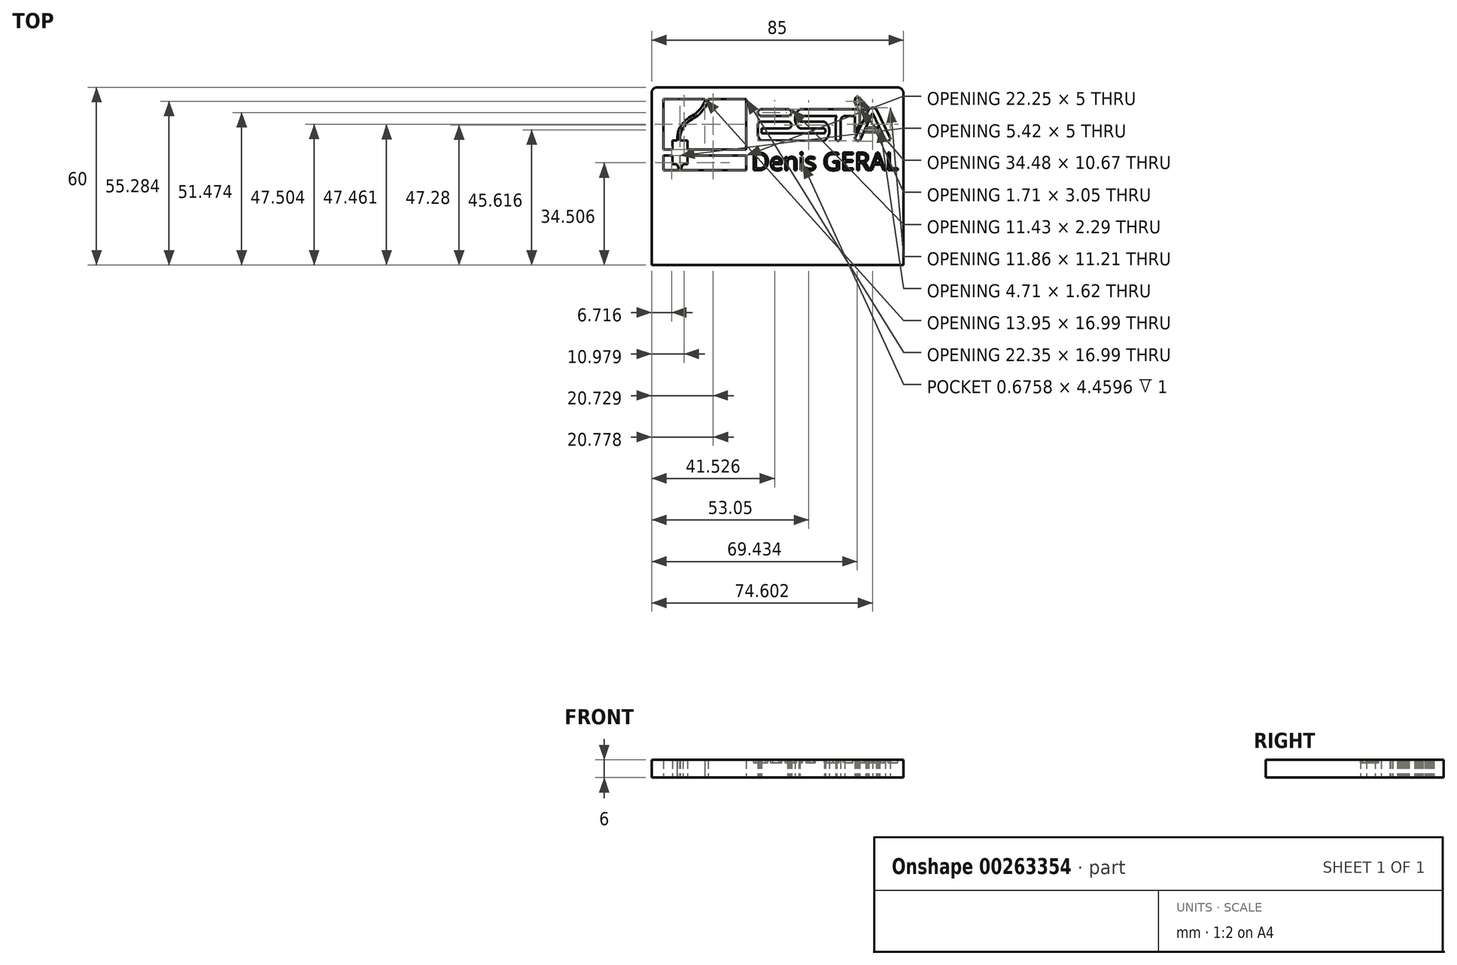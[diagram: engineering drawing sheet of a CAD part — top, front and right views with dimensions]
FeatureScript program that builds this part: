
annotation { "Feature Type Name" : "Feature", "Feature Type Description" : "" }
export const myFeature = defineFeature(function(context is Context, id is Id, definition is map)
    precondition{}
    {
        {
            var Q0;
            Q0=qCreatedBy(makeId("Top.planeOp"),FACE);
            var sketch = newSketch(context, id + "F0", { "sketchPlane" : qUnion([Q0])});
            skLineSegment(sketch, "E0", {"start": v(-259.87, -29.98) * mm, "end": v(-245.92, -29.98) * mm});
            skLineSegment(sketch, "E1", {"start": v(-231.97, -29.98) * mm, "end": v(-231.97, -46.97) * mm});
            skLineSegment(sketch, "E2", {"start": v(-231.97, -46.97) * mm, "end": v(-251.81, -46.97) * mm});
            skLineSegment(sketch, "E3", {"start": v(-251.81, -46.97) * mm, "end": v(-251.81, -43.97) * mm});
            skLineSegment(sketch, "E4", {"start": v(-251.81, -43.97) * mm, "end": v(-254.31, -43.97) * mm});
            skLineSegment(sketch, "E5", {"start": v(-256.81, -43.97) * mm, "end": v(-256.81, -46.97) * mm});
            skLineSegment(sketch, "E6", {"start": v(-256.81, -46.97) * mm, "end": v(-259.87, -46.97) * mm});
            skLineSegment(sketch, "E7", {"start": v(-259.87, -46.97) * mm, "end": v(-259.87, -29.98) * mm});
            skLineSegment(sketch, "E8", {"start": v(-259.87, -48.97) * mm, "end": v(-256.81, -48.97) * mm});
            skLineSegment(sketch, "E9", {"start": v(-256.81, -48.97) * mm, "end": v(-256.81, -51.97) * mm});
            skLineSegment(sketch, "E10", {"start": v(-256.81, -51.97) * mm, "end": v(-255.31, -51.97) * mm});
            skLineSegment(sketch, "E11", {"start": v(-253.31, -51.97) * mm, "end": v(-251.81, -51.97) * mm});
            skLineSegment(sketch, "E12", {"start": v(-251.81, -51.97) * mm, "end": v(-251.81, -48.97) * mm});
            skLineSegment(sketch, "E13", {"start": v(-251.81, -48.97) * mm, "end": v(-231.97, -48.97) * mm});
            skLineSegment(sketch, "E14", {"start": v(-231.97, -48.97) * mm, "end": v(-231.97, -53.97) * mm});
            skLineSegment(sketch, "E15", {"start": v(-259.87, -53.97) * mm, "end": v(-259.87, -48.97) * mm});
            skFitSpline(sketch, "E16", {"points": [v(-255.2, -43.97) * mm, v(-254.45, -39.81) * mm, v(-251.62, -36.46) * mm, v(-248.12, -34) * mm, v(-245.92, -29.98) * mm], "startDerivative": vector(-2.3, 15.03) * mm, "endDerivative": vector(-4.61, 6.78) * mm});
            skFitSpline(sketch, "E17", {"points": [v(-254.31, -43.97) * mm, v(-253.44, -40) * mm, v(-250.75, -37.07) * mm, v(-247.12, -34.45) * mm, v(-244.8, -29.98) * mm], "startDerivative": vector(-2.3, 15.03) * mm, "endDerivative": vector(-4.61, 6.78) * mm});
            skLineSegment(sketch, "E18.bottom", {"start": v(-261.87, -25.98) * mm, "end": v(-180.87, -25.98) * mm});
            skLineSegment(sketch, "E18.top", {"start": v(-263.87, -85.98) * mm, "end": v(-178.87, -85.98) * mm});
            skLineSegment(sketch, "E18.left", {"start": v(-263.87, -27.98) * mm, "end": v(-263.87, -85.98) * mm});
            skLineSegment(sketch, "E18.right", {"start": v(-178.87, -27.98) * mm, "end": v(-178.87, -85.98) * mm});
            skLineSegment(sketch, "E19.trimOffspring", {"start": v(-244.8, -29.98) * mm, "end": v(-231.97, -29.98) * mm});
            skLineSegment(sketch, "E20.trimOffspring", {"start": v(-255.2, -43.97) * mm, "end": v(-256.81, -43.97) * mm});
            skLineSegment(sketch, "E21", {"start": v(-254.31, -53.97) * mm, "end": v(-231.97, -53.97) * mm});
            skLineSegment(sketch, "E22", {"start": v(-254.31, -53.97) * mm, "end": v(-259.87, -53.97) * mm});
            skLineSegment(sketch, "E23.0.0", {"start": v(-226.73, -41.17) * mm, "end": v(-226.73, -39.84) * mm});
            skLineSegment(sketch, "E23.0.1", {"start": v(-226.73, -39.84) * mm, "end": v(-217.96, -39.84) * mm});
            skLineSegment(sketch, "E23.0.2", {"start": v(-217.96, -39.84) * mm, "end": v(-217.85, -39.84) * mm});
            skLineSegment(sketch, "E23.0.3", {"start": v(-217.85, -39.84) * mm, "end": v(-217.73, -39.82) * mm});
            skLineSegment(sketch, "E23.0.4", {"start": v(-217.73, -39.82) * mm, "end": v(-217.62, -39.8) * mm});
            skLineSegment(sketch, "E23.0.5", {"start": v(-217.62, -39.8) * mm, "end": v(-217.5, -39.77) * mm});
            skLineSegment(sketch, "E23.0.6", {"start": v(-217.5, -39.77) * mm, "end": v(-217.4, -39.73) * mm});
            skLineSegment(sketch, "E23.0.7", {"start": v(-217.4, -39.73) * mm, "end": v(-217.3, -39.69) * mm});
            skLineSegment(sketch, "E23.0.8", {"start": v(-217.3, -39.69) * mm, "end": v(-217.2, -39.63) * mm});
            skLineSegment(sketch, "E23.0.9", {"start": v(-217.2, -39.63) * mm, "end": v(-217.1, -39.57) * mm});
            skLineSegment(sketch, "E23.0.10", {"start": v(-217.1, -39.57) * mm, "end": v(-217.02, -39.5) * mm});
            skLineSegment(sketch, "E23.0.11", {"start": v(-217.02, -39.5) * mm, "end": v(-216.94, -39.43) * mm});
            skLineSegment(sketch, "E23.0.12", {"start": v(-216.94, -39.43) * mm, "end": v(-216.87, -39.35) * mm});
            skLineSegment(sketch, "E23.0.13", {"start": v(-216.87, -39.35) * mm, "end": v(-216.8, -39.27) * mm});
            skLineSegment(sketch, "E23.0.14", {"start": v(-216.8, -39.27) * mm, "end": v(-216.75, -39.18) * mm});
            skLineSegment(sketch, "E23.0.15", {"start": v(-216.75, -39.18) * mm, "end": v(-216.7, -39.09) * mm});
            skLineSegment(sketch, "E23.0.16", {"start": v(-216.7, -39.09) * mm, "end": v(-216.67, -39) * mm});
            skLineSegment(sketch, "E23.0.17", {"start": v(-216.67, -39) * mm, "end": v(-216.65, -38.9) * mm});
            skLineSegment(sketch, "E23.0.18", {"start": v(-216.65, -38.9) * mm, "end": v(-216.63, -38.8) * mm});
            skLineSegment(sketch, "E23.0.19", {"start": v(-216.63, -38.8) * mm, "end": v(-216.63, -38.7) * mm});
            skLineSegment(sketch, "E23.0.20", {"start": v(-216.63, -38.7) * mm, "end": v(-216.63, -38.6) * mm});
            skLineSegment(sketch, "E23.0.21", {"start": v(-216.63, -38.6) * mm, "end": v(-216.65, -38.5) * mm});
            skLineSegment(sketch, "E23.0.22", {"start": v(-216.65, -38.5) * mm, "end": v(-216.67, -38.4) * mm});
            skLineSegment(sketch, "E23.0.23", {"start": v(-216.67, -38.4) * mm, "end": v(-216.7, -38.3) * mm});
            skLineSegment(sketch, "E23.0.24", {"start": v(-216.7, -38.3) * mm, "end": v(-216.75, -38.21) * mm});
            skLineSegment(sketch, "E23.0.25", {"start": v(-216.75, -38.21) * mm, "end": v(-216.8, -38.13) * mm});
            skLineSegment(sketch, "E23.0.26", {"start": v(-216.8, -38.13) * mm, "end": v(-216.87, -38.04) * mm});
            skLineSegment(sketch, "E23.0.27", {"start": v(-216.87, -38.04) * mm, "end": v(-216.94, -37.96) * mm});
            skLineSegment(sketch, "E23.0.28", {"start": v(-216.94, -37.96) * mm, "end": v(-217.02, -37.89) * mm});
            skLineSegment(sketch, "E23.0.29", {"start": v(-217.02, -37.89) * mm, "end": v(-217.1, -37.82) * mm});
            skLineSegment(sketch, "E23.0.30", {"start": v(-217.1, -37.82) * mm, "end": v(-217.2, -37.76) * mm});
            skLineSegment(sketch, "E23.0.31", {"start": v(-217.2, -37.76) * mm, "end": v(-217.3, -37.7) * mm});
            skLineSegment(sketch, "E23.0.32", {"start": v(-217.3, -37.7) * mm, "end": v(-217.4, -37.66) * mm});
            skLineSegment(sketch, "E23.0.33", {"start": v(-217.4, -37.66) * mm, "end": v(-217.5, -37.62) * mm});
            skLineSegment(sketch, "E23.0.34", {"start": v(-217.5, -37.62) * mm, "end": v(-217.62, -37.6) * mm});
            skLineSegment(sketch, "E23.0.35", {"start": v(-217.62, -37.6) * mm, "end": v(-217.73, -37.57) * mm});
            skLineSegment(sketch, "E23.0.36", {"start": v(-217.73, -37.57) * mm, "end": v(-217.85, -37.56) * mm});
            skLineSegment(sketch, "E23.0.37", {"start": v(-217.85, -37.56) * mm, "end": v(-217.96, -37.55) * mm});
            skLineSegment(sketch, "E23.0.38", {"start": v(-217.96, -37.55) * mm, "end": v(-226.73, -37.55) * mm});
            skLineSegment(sketch, "E23.0.39", {"start": v(-226.73, -37.55) * mm, "end": v(-226.84, -37.56) * mm});
            skLineSegment(sketch, "E23.0.40", {"start": v(-226.84, -37.56) * mm, "end": v(-226.96, -37.57) * mm});
            skLineSegment(sketch, "E23.0.41", {"start": v(-226.96, -37.57) * mm, "end": v(-227.07, -37.6) * mm});
            skLineSegment(sketch, "E23.0.42", {"start": v(-227.07, -37.6) * mm, "end": v(-227.18, -37.62) * mm});
            skLineSegment(sketch, "E23.0.43", {"start": v(-227.18, -37.62) * mm, "end": v(-227.29, -37.66) * mm});
            skLineSegment(sketch, "E23.0.44", {"start": v(-227.29, -37.66) * mm, "end": v(-227.4, -37.7) * mm});
            skLineSegment(sketch, "E23.0.45", {"start": v(-227.4, -37.7) * mm, "end": v(-227.5, -37.76) * mm});
            skLineSegment(sketch, "E23.0.46", {"start": v(-227.5, -37.76) * mm, "end": v(-227.58, -37.82) * mm});
            skLineSegment(sketch, "E23.0.47", {"start": v(-227.58, -37.82) * mm, "end": v(-227.67, -37.89) * mm});
            skLineSegment(sketch, "E23.0.48", {"start": v(-227.67, -37.89) * mm, "end": v(-227.75, -37.96) * mm});
            skLineSegment(sketch, "E23.0.49", {"start": v(-227.75, -37.96) * mm, "end": v(-227.82, -38.04) * mm});
            skLineSegment(sketch, "E23.0.50", {"start": v(-227.82, -38.04) * mm, "end": v(-227.88, -38.13) * mm});
            skLineSegment(sketch, "E23.0.51", {"start": v(-227.88, -38.13) * mm, "end": v(-227.93, -38.21) * mm});
            skLineSegment(sketch, "E23.0.52", {"start": v(-227.93, -38.21) * mm, "end": v(-227.98, -38.3) * mm});
            skLineSegment(sketch, "E23.0.53", {"start": v(-227.98, -38.3) * mm, "end": v(-228.01, -38.4) * mm});
            skLineSegment(sketch, "E23.0.54", {"start": v(-228.01, -38.4) * mm, "end": v(-228.04, -38.5) * mm});
            skLineSegment(sketch, "E23.0.55", {"start": v(-228.04, -38.5) * mm, "end": v(-228.05, -38.6) * mm});
            skLineSegment(sketch, "E23.0.56", {"start": v(-228.05, -38.6) * mm, "end": v(-228.06, -38.7) * mm});
            skLineSegment(sketch, "E23.0.57", {"start": v(-228.06, -38.7) * mm, "end": v(-228.06, -41.55) * mm});
            skArc(sketch, "E23.0.58", {"start": v(-228.06, -41.55) * mm, "mid": v(-228.06, -41.69) * mm, "end": v(-228.06, -41.82) * mm});
            skArc(sketch, "E23.0.59", {"start": v(-228.06, -41.82) * mm, "mid": v(-227.76, -42.94) * mm, "end": v(-227.01, -43.84) * mm});
            skLineSegment(sketch, "E23.0.60", {"start": v(-227.01, -43.84) * mm, "end": v(-205.58, -44.03) * mm});
            skArc(sketch, "E23.0.61", {"start": v(-205.58, -44.03) * mm, "mid": v(-203.87, -40.8) * mm, "end": v(-205.58, -37.55) * mm});
            skLineSegment(sketch, "E23.0.62", {"start": v(-205.58, -37.55) * mm, "end": v(-213.77, -37.55) * mm});
            skArc(sketch, "E23.0.63", {"start": v(-213.77, -37.55) * mm, "mid": v(-214.15, -36.6) * mm, "end": v(-213.77, -35.65) * mm});
            skLineSegment(sketch, "E23.0.64", {"start": v(-213.77, -35.65) * mm, "end": v(-201.39, -35.65) * mm});
            skArc(sketch, "E23.0.65", {"start": v(-201.39, -35.65) * mm, "mid": v(-201.71, -36.57) * mm, "end": v(-201.77, -37.55) * mm});
            skLineSegment(sketch, "E23.0.66", {"start": v(-201.77, -37.55) * mm, "end": v(-201.77, -43.08) * mm});
            skArc(sketch, "E23.0.67", {"start": v(-201.77, -43.08) * mm, "mid": v(-200.91, -44.04) * mm, "end": v(-200.06, -43.08) * mm});
            skLineSegment(sketch, "E23.0.68", {"start": v(-200.06, -43.08) * mm, "end": v(-200.06, -37.55) * mm});
            skArc(sketch, "E23.0.69", {"start": v(-200.06, -37.55) * mm, "mid": v(-199.78, -36.33) * mm, "end": v(-198.72, -35.65) * mm});
            skLineSegment(sketch, "E23.0.70", {"start": v(-198.72, -35.65) * mm, "end": v(-195.3, -35.65) * mm});
            skLineSegment(sketch, "E23.0.71", {"start": v(-195.3, -35.65) * mm, "end": v(-195.3, -40.41) * mm});
            skArc(sketch, "E23.0.72", {"start": v(-195.3, -40.41) * mm, "mid": v(-195.26, -40.9) * mm, "end": v(-195.1, -41.35) * mm});
            skLineSegment(sketch, "E23.0.73", {"start": v(-195.1, -41.35) * mm, "end": v(-193.58, -38.13) * mm});
            skLineSegment(sketch, "E23.0.74", {"start": v(-193.58, -38.13) * mm, "end": v(-193.58, -34.32) * mm});
            skArc(sketch, "E23.0.75", {"start": v(-193.58, -34.32) * mm, "mid": v(-193.86, -33.64) * mm, "end": v(-194.53, -33.36) * mm});
            skLineSegment(sketch, "E23.0.76", {"start": v(-194.53, -33.36) * mm, "end": v(-213.77, -33.36) * mm});
            skArc(sketch, "E23.0.77", {"start": v(-213.77, -33.36) * mm, "mid": v(-215.49, -36.6) * mm, "end": v(-213.77, -39.84) * mm});
            skLineSegment(sketch, "E23.0.78", {"start": v(-213.77, -39.84) * mm, "end": v(-205.58, -39.84) * mm});
            skArc(sketch, "E23.0.79", {"start": v(-205.58, -39.84) * mm, "mid": v(-205.2, -40.7) * mm, "end": v(-205.58, -41.55) * mm});
            skLineSegment(sketch, "E23.0.80", {"start": v(-205.58, -41.55) * mm, "end": v(-226.34, -41.55) * mm});
            skArc(sketch, "E23.0.81", {"start": v(-226.34, -41.55) * mm, "mid": v(-226.61, -41.44) * mm, "end": v(-226.73, -41.17) * mm});
            skLineSegment(sketch, "E24.0.0", {"start": v(-193.58, -30.54) * mm, "end": v(-193.6, -30.4) * mm});
            skLineSegment(sketch, "E24.0.1", {"start": v(-193.6, -30.4) * mm, "end": v(-193.61, -30.28) * mm});
            skLineSegment(sketch, "E24.0.2", {"start": v(-193.61, -30.28) * mm, "end": v(-193.63, -30.15) * mm});
            skLineSegment(sketch, "E24.0.3", {"start": v(-193.63, -30.15) * mm, "end": v(-193.66, -30.03) * mm});
            skLineSegment(sketch, "E24.0.4", {"start": v(-193.66, -30.03) * mm, "end": v(-193.7, -29.91) * mm});
            skLineSegment(sketch, "E24.0.5", {"start": v(-193.7, -29.91) * mm, "end": v(-193.74, -29.8) * mm});
            skLineSegment(sketch, "E24.0.6", {"start": v(-193.74, -29.8) * mm, "end": v(-193.79, -29.7) * mm});
            skLineSegment(sketch, "E24.0.7", {"start": v(-193.79, -29.7) * mm, "end": v(-193.84, -29.6) * mm});
            skLineSegment(sketch, "E24.0.8", {"start": v(-193.84, -29.6) * mm, "end": v(-193.9, -29.51) * mm});
            skLineSegment(sketch, "E24.0.9", {"start": v(-193.9, -29.51) * mm, "end": v(-193.96, -29.43) * mm});
            skLineSegment(sketch, "E24.0.10", {"start": v(-193.96, -29.43) * mm, "end": v(-194.02, -29.36) * mm});
            skLineSegment(sketch, "E24.0.11", {"start": v(-194.02, -29.36) * mm, "end": v(-194.09, -29.3) * mm});
            skLineSegment(sketch, "E24.0.12", {"start": v(-194.09, -29.3) * mm, "end": v(-194.16, -29.26) * mm});
            skLineSegment(sketch, "E24.0.13", {"start": v(-194.16, -29.26) * mm, "end": v(-194.23, -29.22) * mm});
            skLineSegment(sketch, "E24.0.14", {"start": v(-194.23, -29.22) * mm, "end": v(-194.3, -29.2) * mm});
            skLineSegment(sketch, "E24.0.15", {"start": v(-194.3, -29.2) * mm, "end": v(-194.37, -29.18) * mm});
            skLineSegment(sketch, "E24.0.16", {"start": v(-194.37, -29.18) * mm, "end": v(-194.45, -29.17) * mm});
            skLineSegment(sketch, "E24.0.17", {"start": v(-194.45, -29.17) * mm, "end": v(-194.52, -29.18) * mm});
            skLineSegment(sketch, "E24.0.18", {"start": v(-194.52, -29.18) * mm, "end": v(-194.6, -29.2) * mm});
            skLineSegment(sketch, "E24.0.19", {"start": v(-194.6, -29.2) * mm, "end": v(-194.67, -29.23) * mm});
            skLineSegment(sketch, "E24.0.20", {"start": v(-194.67, -29.23) * mm, "end": v(-194.74, -29.27) * mm});
            skLineSegment(sketch, "E24.0.21", {"start": v(-194.74, -29.27) * mm, "end": v(-194.81, -29.33) * mm});
            skLineSegment(sketch, "E24.0.22", {"start": v(-194.81, -29.33) * mm, "end": v(-194.88, -29.39) * mm});
            skLineSegment(sketch, "E24.0.23", {"start": v(-194.88, -29.39) * mm, "end": v(-194.94, -29.46) * mm});
            skLineSegment(sketch, "E24.0.24", {"start": v(-194.94, -29.46) * mm, "end": v(-195, -29.54) * mm});
            skLineSegment(sketch, "E24.0.25", {"start": v(-195, -29.54) * mm, "end": v(-195.05, -29.64) * mm});
            skLineSegment(sketch, "E24.0.26", {"start": v(-195.05, -29.64) * mm, "end": v(-195.1, -29.74) * mm});
            skLineSegment(sketch, "E24.0.27", {"start": v(-195.1, -29.74) * mm, "end": v(-195.15, -29.84) * mm});
            skLineSegment(sketch, "E24.0.28", {"start": v(-195.15, -29.84) * mm, "end": v(-195.18, -29.96) * mm});
            skLineSegment(sketch, "E24.0.29", {"start": v(-195.18, -29.96) * mm, "end": v(-195.22, -30.07) * mm});
            skLineSegment(sketch, "E24.0.30", {"start": v(-195.22, -30.07) * mm, "end": v(-195.25, -30.2) * mm});
            skLineSegment(sketch, "E24.0.31", {"start": v(-195.25, -30.2) * mm, "end": v(-195.27, -30.33) * mm});
            skLineSegment(sketch, "E24.0.32", {"start": v(-195.27, -30.33) * mm, "end": v(-195.28, -30.46) * mm});
            skLineSegment(sketch, "E24.0.33", {"start": v(-195.28, -30.46) * mm, "end": v(-195.3, -30.59) * mm});
            skLineSegment(sketch, "E24.0.34", {"start": v(-195.3, -30.59) * mm, "end": v(-195.3, -30.72) * mm});
            skLineSegment(sketch, "E24.0.35", {"start": v(-195.3, -30.72) * mm, "end": v(-195.29, -30.85) * mm});
            skLineSegment(sketch, "E24.0.36", {"start": v(-195.29, -30.85) * mm, "end": v(-195.28, -30.99) * mm});
            skLineSegment(sketch, "E24.0.37", {"start": v(-195.28, -30.99) * mm, "end": v(-195.26, -31.11) * mm});
            skLineSegment(sketch, "E24.0.38", {"start": v(-195.26, -31.11) * mm, "end": v(-195.24, -31.24) * mm});
            skLineSegment(sketch, "E24.0.39", {"start": v(-195.24, -31.24) * mm, "end": v(-195.2, -31.36) * mm});
            skLineSegment(sketch, "E24.0.40", {"start": v(-195.2, -31.36) * mm, "end": v(-195.17, -31.48) * mm});
            skLineSegment(sketch, "E24.0.41", {"start": v(-195.17, -31.48) * mm, "end": v(-195.13, -31.6) * mm});
            skLineSegment(sketch, "E24.0.42", {"start": v(-195.13, -31.6) * mm, "end": v(-195.08, -31.7) * mm});
            skLineSegment(sketch, "E24.0.43", {"start": v(-195.08, -31.7) * mm, "end": v(-195.03, -31.8) * mm});
            skLineSegment(sketch, "E24.0.44", {"start": v(-195.03, -31.8) * mm, "end": v(-194.98, -31.88) * mm});
            skLineSegment(sketch, "E24.0.45", {"start": v(-194.98, -31.88) * mm, "end": v(-194.92, -31.96) * mm});
            skLineSegment(sketch, "E24.0.46", {"start": v(-194.92, -31.96) * mm, "end": v(-194.85, -32.03) * mm});
            skLineSegment(sketch, "E24.0.47", {"start": v(-194.85, -32.03) * mm, "end": v(-194.79, -32.09) * mm});
            skLineSegment(sketch, "E24.0.48", {"start": v(-194.79, -32.09) * mm, "end": v(-194.72, -32.14) * mm});
            skLineSegment(sketch, "E24.0.49", {"start": v(-194.72, -32.14) * mm, "end": v(-194.64, -32.17) * mm});
            skLineSegment(sketch, "E24.0.50", {"start": v(-194.64, -32.17) * mm, "end": v(-194.57, -32.2) * mm});
            skLineSegment(sketch, "E24.0.51", {"start": v(-194.57, -32.2) * mm, "end": v(-194.5, -32.22) * mm});
            skLineSegment(sketch, "E24.0.52", {"start": v(-194.5, -32.22) * mm, "end": v(-194.42, -32.22) * mm});
            skLineSegment(sketch, "E24.0.53", {"start": v(-194.42, -32.22) * mm, "end": v(-194.35, -32.21) * mm});
            skLineSegment(sketch, "E24.0.54", {"start": v(-194.35, -32.21) * mm, "end": v(-194.27, -32.2) * mm});
            skLineSegment(sketch, "E24.0.55", {"start": v(-194.27, -32.2) * mm, "end": v(-194.2, -32.16) * mm});
            skLineSegment(sketch, "E24.0.56", {"start": v(-194.2, -32.16) * mm, "end": v(-194.13, -32.12) * mm});
            skLineSegment(sketch, "E24.0.57", {"start": v(-194.13, -32.12) * mm, "end": v(-194.06, -32.07) * mm});
            skLineSegment(sketch, "E24.0.58", {"start": v(-194.06, -32.07) * mm, "end": v(-194, -32) * mm});
            skLineSegment(sketch, "E24.0.59", {"start": v(-194, -32) * mm, "end": v(-193.93, -31.93) * mm});
            skLineSegment(sketch, "E24.0.60", {"start": v(-193.93, -31.93) * mm, "end": v(-193.87, -31.85) * mm});
            skLineSegment(sketch, "E24.0.61", {"start": v(-193.87, -31.85) * mm, "end": v(-193.82, -31.76) * mm});
            skLineSegment(sketch, "E24.0.62", {"start": v(-193.82, -31.76) * mm, "end": v(-193.77, -31.66) * mm});
            skLineSegment(sketch, "E24.0.63", {"start": v(-193.77, -31.66) * mm, "end": v(-193.73, -31.55) * mm});
            skLineSegment(sketch, "E24.0.64", {"start": v(-193.73, -31.55) * mm, "end": v(-193.69, -31.44) * mm});
            skLineSegment(sketch, "E24.0.65", {"start": v(-193.69, -31.44) * mm, "end": v(-193.65, -31.32) * mm});
            skLineSegment(sketch, "E24.0.66", {"start": v(-193.65, -31.32) * mm, "end": v(-193.63, -31.2) * mm});
            skLineSegment(sketch, "E24.0.67", {"start": v(-193.63, -31.2) * mm, "end": v(-193.6, -31.07) * mm});
            skLineSegment(sketch, "E24.0.68", {"start": v(-193.6, -31.07) * mm, "end": v(-193.59, -30.94) * mm});
            skLineSegment(sketch, "E24.0.69", {"start": v(-193.59, -30.94) * mm, "end": v(-193.58, -30.8) * mm});
            skLineSegment(sketch, "E24.0.70", {"start": v(-193.58, -30.8) * mm, "end": v(-193.58, -30.67) * mm});
            skLineSegment(sketch, "E24.0.71", {"start": v(-193.58, -30.67) * mm, "end": v(-193.58, -30.54) * mm});
            skLineSegment(sketch, "E25.0.0", {"start": v(-226.96, -35.63) * mm, "end": v(-226.84, -35.64) * mm});
            skLineSegment(sketch, "E25.0.1", {"start": v(-226.84, -35.64) * mm, "end": v(-226.73, -35.65) * mm});
            skLineSegment(sketch, "E25.0.2", {"start": v(-226.73, -35.65) * mm, "end": v(-217.96, -35.65) * mm});
            skLineSegment(sketch, "E25.0.3", {"start": v(-217.96, -35.65) * mm, "end": v(-217.85, -35.64) * mm});
            skLineSegment(sketch, "E25.0.4", {"start": v(-217.85, -35.64) * mm, "end": v(-217.73, -35.63) * mm});
            skLineSegment(sketch, "E25.0.5", {"start": v(-217.73, -35.63) * mm, "end": v(-217.62, -35.61) * mm});
            skLineSegment(sketch, "E25.0.6", {"start": v(-217.62, -35.61) * mm, "end": v(-217.5, -35.58) * mm});
            skLineSegment(sketch, "E25.0.7", {"start": v(-217.5, -35.58) * mm, "end": v(-217.4, -35.54) * mm});
            skLineSegment(sketch, "E25.0.8", {"start": v(-217.4, -35.54) * mm, "end": v(-217.3, -35.5) * mm});
            skLineSegment(sketch, "E25.0.9", {"start": v(-217.3, -35.5) * mm, "end": v(-217.2, -35.44) * mm});
            skLineSegment(sketch, "E25.0.10", {"start": v(-217.2, -35.44) * mm, "end": v(-217.1, -35.38) * mm});
            skLineSegment(sketch, "E25.0.11", {"start": v(-217.1, -35.38) * mm, "end": v(-217.02, -35.31) * mm});
            skLineSegment(sketch, "E25.0.12", {"start": v(-217.02, -35.31) * mm, "end": v(-216.94, -35.24) * mm});
            skLineSegment(sketch, "E25.0.13", {"start": v(-216.94, -35.24) * mm, "end": v(-216.87, -35.16) * mm});
            skLineSegment(sketch, "E25.0.14", {"start": v(-216.87, -35.16) * mm, "end": v(-216.8, -35.08) * mm});
            skLineSegment(sketch, "E25.0.15", {"start": v(-216.8, -35.08) * mm, "end": v(-216.75, -34.99) * mm});
            skLineSegment(sketch, "E25.0.16", {"start": v(-216.75, -34.99) * mm, "end": v(-216.7, -34.9) * mm});
            skLineSegment(sketch, "E25.0.17", {"start": v(-216.7, -34.9) * mm, "end": v(-216.67, -34.8) * mm});
            skLineSegment(sketch, "E25.0.18", {"start": v(-216.67, -34.8) * mm, "end": v(-216.65, -34.7) * mm});
            skLineSegment(sketch, "E25.0.19", {"start": v(-216.65, -34.7) * mm, "end": v(-216.63, -34.6) * mm});
            skLineSegment(sketch, "E25.0.20", {"start": v(-216.63, -34.6) * mm, "end": v(-216.63, -34.5) * mm});
            skLineSegment(sketch, "E25.0.21", {"start": v(-216.63, -34.5) * mm, "end": v(-216.63, -34.4) * mm});
            skLineSegment(sketch, "E25.0.22", {"start": v(-216.63, -34.4) * mm, "end": v(-216.65, -34.3) * mm});
            skLineSegment(sketch, "E25.0.23", {"start": v(-216.65, -34.3) * mm, "end": v(-216.67, -34.21) * mm});
            skLineSegment(sketch, "E25.0.24", {"start": v(-216.67, -34.21) * mm, "end": v(-216.7, -34.12) * mm});
            skLineSegment(sketch, "E25.0.25", {"start": v(-216.7, -34.12) * mm, "end": v(-216.75, -34.02) * mm});
            skLineSegment(sketch, "E25.0.26", {"start": v(-216.75, -34.02) * mm, "end": v(-216.8, -33.93) * mm});
            skLineSegment(sketch, "E25.0.27", {"start": v(-216.8, -33.93) * mm, "end": v(-216.87, -33.85) * mm});
            skLineSegment(sketch, "E25.0.28", {"start": v(-216.87, -33.85) * mm, "end": v(-216.94, -33.77) * mm});
            skLineSegment(sketch, "E25.0.29", {"start": v(-216.94, -33.77) * mm, "end": v(-217.02, -33.7) * mm});
            skLineSegment(sketch, "E25.0.30", {"start": v(-217.02, -33.7) * mm, "end": v(-217.1, -33.63) * mm});
            skLineSegment(sketch, "E25.0.31", {"start": v(-217.1, -33.63) * mm, "end": v(-217.2, -33.57) * mm});
            skLineSegment(sketch, "E25.0.32", {"start": v(-217.2, -33.57) * mm, "end": v(-217.3, -33.52) * mm});
            skLineSegment(sketch, "E25.0.33", {"start": v(-217.3, -33.52) * mm, "end": v(-217.4, -33.47) * mm});
            skLineSegment(sketch, "E25.0.34", {"start": v(-217.4, -33.47) * mm, "end": v(-217.5, -33.43) * mm});
            skLineSegment(sketch, "E25.0.35", {"start": v(-217.5, -33.43) * mm, "end": v(-217.62, -33.4) * mm});
            skLineSegment(sketch, "E25.0.36", {"start": v(-217.62, -33.4) * mm, "end": v(-217.73, -33.38) * mm});
            skLineSegment(sketch, "E25.0.37", {"start": v(-217.73, -33.38) * mm, "end": v(-217.85, -33.37) * mm});
            skLineSegment(sketch, "E25.0.38", {"start": v(-217.85, -33.37) * mm, "end": v(-217.96, -33.36) * mm});
            skLineSegment(sketch, "E25.0.39", {"start": v(-217.96, -33.36) * mm, "end": v(-226.73, -33.36) * mm});
            skLineSegment(sketch, "E25.0.40", {"start": v(-226.73, -33.36) * mm, "end": v(-226.84, -33.37) * mm});
            skLineSegment(sketch, "E25.0.41", {"start": v(-226.84, -33.37) * mm, "end": v(-226.96, -33.38) * mm});
            skLineSegment(sketch, "E25.0.42", {"start": v(-226.96, -33.38) * mm, "end": v(-227.07, -33.4) * mm});
            skLineSegment(sketch, "E25.0.43", {"start": v(-227.07, -33.4) * mm, "end": v(-227.18, -33.43) * mm});
            skLineSegment(sketch, "E25.0.44", {"start": v(-227.18, -33.43) * mm, "end": v(-227.29, -33.47) * mm});
            skLineSegment(sketch, "E25.0.45", {"start": v(-227.29, -33.47) * mm, "end": v(-227.4, -33.52) * mm});
            skLineSegment(sketch, "E25.0.46", {"start": v(-227.4, -33.52) * mm, "end": v(-227.5, -33.57) * mm});
            skLineSegment(sketch, "E25.0.47", {"start": v(-227.5, -33.57) * mm, "end": v(-227.58, -33.63) * mm});
            skLineSegment(sketch, "E25.0.48", {"start": v(-227.58, -33.63) * mm, "end": v(-227.67, -33.7) * mm});
            skLineSegment(sketch, "E25.0.49", {"start": v(-227.67, -33.7) * mm, "end": v(-227.75, -33.77) * mm});
            skLineSegment(sketch, "E25.0.50", {"start": v(-227.75, -33.77) * mm, "end": v(-227.82, -33.85) * mm});
            skLineSegment(sketch, "E25.0.51", {"start": v(-227.82, -33.85) * mm, "end": v(-227.88, -33.93) * mm});
            skLineSegment(sketch, "E25.0.52", {"start": v(-227.88, -33.93) * mm, "end": v(-227.93, -34.02) * mm});
            skLineSegment(sketch, "E25.0.53", {"start": v(-227.93, -34.02) * mm, "end": v(-227.98, -34.12) * mm});
            skLineSegment(sketch, "E25.0.54", {"start": v(-227.98, -34.12) * mm, "end": v(-228.01, -34.21) * mm});
            skLineSegment(sketch, "E25.0.55", {"start": v(-228.01, -34.21) * mm, "end": v(-228.04, -34.3) * mm});
            skLineSegment(sketch, "E25.0.56", {"start": v(-228.04, -34.3) * mm, "end": v(-228.05, -34.4) * mm});
            skLineSegment(sketch, "E25.0.57", {"start": v(-228.05, -34.4) * mm, "end": v(-228.06, -34.5) * mm});
            skLineSegment(sketch, "E25.0.58", {"start": v(-228.06, -34.5) * mm, "end": v(-228.05, -34.6) * mm});
            skLineSegment(sketch, "E25.0.59", {"start": v(-228.05, -34.6) * mm, "end": v(-228.04, -34.7) * mm});
            skLineSegment(sketch, "E25.0.60", {"start": v(-228.04, -34.7) * mm, "end": v(-228.01, -34.8) * mm});
            skLineSegment(sketch, "E25.0.61", {"start": v(-228.01, -34.8) * mm, "end": v(-227.98, -34.9) * mm});
            skLineSegment(sketch, "E25.0.62", {"start": v(-227.98, -34.9) * mm, "end": v(-227.93, -34.99) * mm});
            skLineSegment(sketch, "E25.0.63", {"start": v(-227.93, -34.99) * mm, "end": v(-227.88, -35.08) * mm});
            skLineSegment(sketch, "E25.0.64", {"start": v(-227.88, -35.08) * mm, "end": v(-227.82, -35.16) * mm});
            skLineSegment(sketch, "E25.0.65", {"start": v(-227.82, -35.16) * mm, "end": v(-227.75, -35.24) * mm});
            skLineSegment(sketch, "E25.0.66", {"start": v(-227.75, -35.24) * mm, "end": v(-227.67, -35.31) * mm});
            skLineSegment(sketch, "E25.0.67", {"start": v(-227.67, -35.31) * mm, "end": v(-227.58, -35.38) * mm});
            skLineSegment(sketch, "E25.0.68", {"start": v(-227.58, -35.38) * mm, "end": v(-227.5, -35.44) * mm});
            skLineSegment(sketch, "E25.0.69", {"start": v(-227.5, -35.44) * mm, "end": v(-227.4, -35.5) * mm});
            skLineSegment(sketch, "E25.0.70", {"start": v(-227.4, -35.5) * mm, "end": v(-227.29, -35.54) * mm});
            skLineSegment(sketch, "E25.0.71", {"start": v(-227.29, -35.54) * mm, "end": v(-227.18, -35.58) * mm});
            skLineSegment(sketch, "E25.0.72", {"start": v(-227.18, -35.58) * mm, "end": v(-227.07, -35.61) * mm});
            skLineSegment(sketch, "E25.0.73", {"start": v(-227.07, -35.61) * mm, "end": v(-226.96, -35.63) * mm});
            skLineSegment(sketch, "E26.0.0", {"start": v(-189.27, -34.68) * mm, "end": v(-184.91, -43.85) * mm});
            skArc(sketch, "E26.0.1", {"start": v(-184.91, -43.85) * mm, "mid": v(-183.88, -44.05) * mm, "end": v(-183.34, -43.15) * mm});
            skLineSegment(sketch, "E26.0.2", {"start": v(-183.34, -43.15) * mm, "end": v(-187.97, -33.37) * mm});
            skArc(sketch, "E26.0.3", {"start": v(-187.97, -33.37) * mm, "mid": v(-189.26, -32.91) * mm, "end": v(-190.55, -33.38) * mm});
            skLineSegment(sketch, "E26.0.4", {"start": v(-190.55, -33.38) * mm, "end": v(-195.2, -43.17) * mm});
            skArc(sketch, "E26.0.5", {"start": v(-195.2, -43.17) * mm, "mid": v(-194.62, -44) * mm, "end": v(-193.63, -43.88) * mm});
            skLineSegment(sketch, "E26.0.6", {"start": v(-193.63, -43.88) * mm, "end": v(-189.27, -34.68) * mm});
            skLineSegment(sketch, "E27.0.0", {"start": v(-190.96, -41.16) * mm, "end": v(-190.9, -41.17) * mm});
            skLineSegment(sketch, "E27.0.1", {"start": v(-190.9, -41.17) * mm, "end": v(-190.82, -41.17) * mm});
            skLineSegment(sketch, "E27.0.2", {"start": v(-190.82, -41.17) * mm, "end": v(-187.71, -41.17) * mm});
            skLineSegment(sketch, "E27.0.3", {"start": v(-187.71, -41.17) * mm, "end": v(-187.64, -41.17) * mm});
            skLineSegment(sketch, "E27.0.4", {"start": v(-187.64, -41.17) * mm, "end": v(-187.57, -41.16) * mm});
            skLineSegment(sketch, "E27.0.5", {"start": v(-187.57, -41.16) * mm, "end": v(-187.5, -41.15) * mm});
            skLineSegment(sketch, "E27.0.6", {"start": v(-187.5, -41.15) * mm, "end": v(-187.44, -41.12) * mm});
            skLineSegment(sketch, "E27.0.7", {"start": v(-187.44, -41.12) * mm, "end": v(-187.37, -41.1) * mm});
            skLineSegment(sketch, "E27.0.8", {"start": v(-187.37, -41.1) * mm, "end": v(-187.31, -41.06) * mm});
            skLineSegment(sketch, "E27.0.9", {"start": v(-187.31, -41.06) * mm, "end": v(-187.25, -41.03) * mm});
            skLineSegment(sketch, "E27.0.10", {"start": v(-187.25, -41.03) * mm, "end": v(-187.2, -40.98) * mm});
            skLineSegment(sketch, "E27.0.11", {"start": v(-187.2, -40.98) * mm, "end": v(-187.15, -40.94) * mm});
            skLineSegment(sketch, "E27.0.12", {"start": v(-187.15, -40.94) * mm, "end": v(-187.1, -40.88) * mm});
            skLineSegment(sketch, "E27.0.13", {"start": v(-187.1, -40.88) * mm, "end": v(-187.06, -40.83) * mm});
            skLineSegment(sketch, "E27.0.14", {"start": v(-187.06, -40.83) * mm, "end": v(-187.02, -40.77) * mm});
            skLineSegment(sketch, "E27.0.15", {"start": v(-187.02, -40.77) * mm, "end": v(-186.99, -40.7) * mm});
            skLineSegment(sketch, "E27.0.16", {"start": v(-186.99, -40.7) * mm, "end": v(-186.96, -40.64) * mm});
            skLineSegment(sketch, "E27.0.17", {"start": v(-186.96, -40.64) * mm, "end": v(-186.94, -40.57) * mm});
            skLineSegment(sketch, "E27.0.18", {"start": v(-186.94, -40.57) * mm, "end": v(-186.92, -40.5) * mm});
            skLineSegment(sketch, "E27.0.19", {"start": v(-186.92, -40.5) * mm, "end": v(-186.91, -40.43) * mm});
            skLineSegment(sketch, "E27.0.20", {"start": v(-186.91, -40.43) * mm, "end": v(-186.91, -40.36) * mm});
            skLineSegment(sketch, "E27.0.21", {"start": v(-186.91, -40.36) * mm, "end": v(-186.91, -40.3) * mm});
            skLineSegment(sketch, "E27.0.22", {"start": v(-186.91, -40.3) * mm, "end": v(-186.92, -40.22) * mm});
            skLineSegment(sketch, "E27.0.23", {"start": v(-186.92, -40.22) * mm, "end": v(-186.94, -40.15) * mm});
            skLineSegment(sketch, "E27.0.24", {"start": v(-186.94, -40.15) * mm, "end": v(-186.96, -40.09) * mm});
            skLineSegment(sketch, "E27.0.25", {"start": v(-186.96, -40.09) * mm, "end": v(-186.99, -40.02) * mm});
            skLineSegment(sketch, "E27.0.26", {"start": v(-186.99, -40.02) * mm, "end": v(-187.02, -39.96) * mm});
            skLineSegment(sketch, "E27.0.27", {"start": v(-187.02, -39.96) * mm, "end": v(-187.06, -39.9) * mm});
            skLineSegment(sketch, "E27.0.28", {"start": v(-187.06, -39.9) * mm, "end": v(-187.1, -39.84) * mm});
            skLineSegment(sketch, "E27.0.29", {"start": v(-187.1, -39.84) * mm, "end": v(-187.15, -39.8) * mm});
            skLineSegment(sketch, "E27.0.30", {"start": v(-187.15, -39.8) * mm, "end": v(-187.2, -39.74) * mm});
            skLineSegment(sketch, "E27.0.31", {"start": v(-187.2, -39.74) * mm, "end": v(-187.25, -39.7) * mm});
            skLineSegment(sketch, "E27.0.32", {"start": v(-187.25, -39.7) * mm, "end": v(-187.31, -39.66) * mm});
            skLineSegment(sketch, "E27.0.33", {"start": v(-187.31, -39.66) * mm, "end": v(-187.37, -39.63) * mm});
            skLineSegment(sketch, "E27.0.34", {"start": v(-187.37, -39.63) * mm, "end": v(-187.44, -39.6) * mm});
            skLineSegment(sketch, "E27.0.35", {"start": v(-187.44, -39.6) * mm, "end": v(-187.5, -39.58) * mm});
            skLineSegment(sketch, "E27.0.36", {"start": v(-187.5, -39.58) * mm, "end": v(-187.57, -39.57) * mm});
            skLineSegment(sketch, "E27.0.37", {"start": v(-187.57, -39.57) * mm, "end": v(-187.64, -39.56) * mm});
            skLineSegment(sketch, "E27.0.38", {"start": v(-187.64, -39.56) * mm, "end": v(-187.71, -39.55) * mm});
            skLineSegment(sketch, "E27.0.39", {"start": v(-187.71, -39.55) * mm, "end": v(-190.82, -39.55) * mm});
            skLineSegment(sketch, "E27.0.40", {"start": v(-190.82, -39.55) * mm, "end": v(-190.9, -39.56) * mm});
            skLineSegment(sketch, "E27.0.41", {"start": v(-190.9, -39.56) * mm, "end": v(-190.96, -39.57) * mm});
            skLineSegment(sketch, "E27.0.42", {"start": v(-190.96, -39.57) * mm, "end": v(-191.03, -39.58) * mm});
            skLineSegment(sketch, "E27.0.43", {"start": v(-191.03, -39.58) * mm, "end": v(-191.1, -39.6) * mm});
            skLineSegment(sketch, "E27.0.44", {"start": v(-191.1, -39.6) * mm, "end": v(-191.16, -39.63) * mm});
            skLineSegment(sketch, "E27.0.45", {"start": v(-191.16, -39.63) * mm, "end": v(-191.22, -39.66) * mm});
            skLineSegment(sketch, "E27.0.46", {"start": v(-191.22, -39.66) * mm, "end": v(-191.28, -39.7) * mm});
            skLineSegment(sketch, "E27.0.47", {"start": v(-191.28, -39.7) * mm, "end": v(-191.34, -39.74) * mm});
            skLineSegment(sketch, "E27.0.48", {"start": v(-191.34, -39.74) * mm, "end": v(-191.4, -39.8) * mm});
            skLineSegment(sketch, "E27.0.49", {"start": v(-191.4, -39.8) * mm, "end": v(-191.44, -39.84) * mm});
            skLineSegment(sketch, "E27.0.50", {"start": v(-191.44, -39.84) * mm, "end": v(-191.48, -39.9) * mm});
            skLineSegment(sketch, "E27.0.51", {"start": v(-191.48, -39.9) * mm, "end": v(-191.52, -39.96) * mm});
            skLineSegment(sketch, "E27.0.52", {"start": v(-191.52, -39.96) * mm, "end": v(-191.55, -40.02) * mm});
            skLineSegment(sketch, "E27.0.53", {"start": v(-191.55, -40.02) * mm, "end": v(-191.58, -40.09) * mm});
            skLineSegment(sketch, "E27.0.54", {"start": v(-191.58, -40.09) * mm, "end": v(-191.6, -40.15) * mm});
            skLineSegment(sketch, "E27.0.55", {"start": v(-191.6, -40.15) * mm, "end": v(-191.61, -40.22) * mm});
            skLineSegment(sketch, "E27.0.56", {"start": v(-191.61, -40.22) * mm, "end": v(-191.62, -40.3) * mm});
            skLineSegment(sketch, "E27.0.57", {"start": v(-191.62, -40.3) * mm, "end": v(-191.63, -40.36) * mm});
            skLineSegment(sketch, "E27.0.58", {"start": v(-191.63, -40.36) * mm, "end": v(-191.62, -40.43) * mm});
            skLineSegment(sketch, "E27.0.59", {"start": v(-191.62, -40.43) * mm, "end": v(-191.61, -40.5) * mm});
            skLineSegment(sketch, "E27.0.60", {"start": v(-191.61, -40.5) * mm, "end": v(-191.6, -40.57) * mm});
            skLineSegment(sketch, "E27.0.61", {"start": v(-191.6, -40.57) * mm, "end": v(-191.58, -40.64) * mm});
            skLineSegment(sketch, "E27.0.62", {"start": v(-191.58, -40.64) * mm, "end": v(-191.55, -40.7) * mm});
            skLineSegment(sketch, "E27.0.63", {"start": v(-191.55, -40.7) * mm, "end": v(-191.52, -40.77) * mm});
            skLineSegment(sketch, "E27.0.64", {"start": v(-191.52, -40.77) * mm, "end": v(-191.48, -40.83) * mm});
            skLineSegment(sketch, "E27.0.65", {"start": v(-191.48, -40.83) * mm, "end": v(-191.44, -40.88) * mm});
            skLineSegment(sketch, "E27.0.66", {"start": v(-191.44, -40.88) * mm, "end": v(-191.4, -40.94) * mm});
            skLineSegment(sketch, "E27.0.67", {"start": v(-191.4, -40.94) * mm, "end": v(-191.34, -40.98) * mm});
            skLineSegment(sketch, "E27.0.68", {"start": v(-191.34, -40.98) * mm, "end": v(-191.28, -41.03) * mm});
            skLineSegment(sketch, "E27.0.69", {"start": v(-191.28, -41.03) * mm, "end": v(-191.22, -41.06) * mm});
            skLineSegment(sketch, "E27.0.70", {"start": v(-191.22, -41.06) * mm, "end": v(-191.16, -41.1) * mm});
            skLineSegment(sketch, "E27.0.71", {"start": v(-191.16, -41.1) * mm, "end": v(-191.1, -41.12) * mm});
            skLineSegment(sketch, "E27.0.72", {"start": v(-191.1, -41.12) * mm, "end": v(-191.03, -41.15) * mm});
            skLineSegment(sketch, "E27.0.73", {"start": v(-191.03, -41.15) * mm, "end": v(-190.96, -41.16) * mm});
            skLineSegment(sketch, "E28", {"start": v(-255.31, -51.97) * mm, "end": v(-254.44, -53.97) * mm});
            skLineSegment(sketch, "E29", {"start": v(-253.31, -51.97) * mm, "end": v(-254.22, -53.97) * mm});
            skPoint(sketch, "E30.visualSharp", {"position": v(-178.87, -25.98) * mm});
            skArc(sketch, "E30.filletArc", {"start": v(-178.87, -27.98) * mm, "mid": v(-179.45, -26.56) * mm, "end": v(-180.87, -25.98) * mm});
            skPoint(sketch, "E31.visualSharp", {"position": v(-263.87, -25.98) * mm});
            skArc(sketch, "E31.filletArc", {"start": v(-261.87, -25.98) * mm, "mid": v(-263.28, -26.56) * mm, "end": v(-263.87, -27.98) * mm});
            skSolve(sketch);
        }
        {
            var Q0;
            Q0 = qSketchRegion(id + "F0", true);
            extrude(context, id + "F1", {"entities" : qUnion([Q0]), "depth" : 6 * mm});
        }
        {
            var Q0;
            Q0=makeQuery(id+"F1.opExtrude","CAP_FACE",FACE,{"disambiguationData":[OSD([sQuery(id+"F0.wireOp",EDGE,"E0"),sQuery(id+"F0.wireOp",EDGE,"E1"),sQuery(id+"F0.wireOp",EDGE,"E2"),sQuery(id+"F0.wireOp",EDGE,"E3"),sQuery(id+"F0.wireOp",EDGE,"E4"),sQuery(id+"F0.wireOp",EDGE,"E5"),sQuery(id+"F0.wireOp",EDGE,"E6"),sQuery(id+"F0.wireOp",EDGE,"E7"),sQuery(id+"F0.wireOp",EDGE,"E8"),sQuery(id+"F0.wireOp",EDGE,"E9"),sQuery(id+"F0.wireOp",EDGE,"E10"),sQuery(id+"F0.wireOp",EDGE,"E11"),sQuery(id+"F0.wireOp",EDGE,"E12"),sQuery(id+"F0.wireOp",EDGE,"E13"),sQuery(id+"F0.wireOp",EDGE,"E14"),sQuery(id+"F0.wireOp",EDGE,"E15"),sQuery(id+"F0.wireOp",EDGE,"E16"),sQuery(id+"F0.wireOp",EDGE,"E17"),sQuery(id+"F0.wireOp",EDGE,"E18.bottom"),sQuery(id+"F0.wireOp",EDGE,"E18.top"),sQuery(id+"F0.wireOp",EDGE,"E18.left"),sQuery(id+"F0.wireOp",EDGE,"E18.right"),sQuery(id+"F0.wireOp",EDGE,"E19.trimOffspring"),sQuery(id+"F0.wireOp",EDGE,"E20.trimOffspring"),sQuery(id+"F0.wireOp",EDGE,"E21"),sQuery(id+"F0.wireOp",EDGE,"E22"),sQuery(id+"F0.wireOp",EDGE,"E23.0.0"),sQuery(id+"F0.wireOp",EDGE,"E23.0.1"),sQuery(id+"F0.wireOp",EDGE,"E23.0.2"),sQuery(id+"F0.wireOp",EDGE,"E23.0.3"),sQuery(id+"F0.wireOp",EDGE,"E23.0.4"),sQuery(id+"F0.wireOp",EDGE,"E23.0.5"),sQuery(id+"F0.wireOp",EDGE,"E23.0.6"),sQuery(id+"F0.wireOp",EDGE,"E23.0.7"),sQuery(id+"F0.wireOp",EDGE,"E23.0.8"),sQuery(id+"F0.wireOp",EDGE,"E23.0.9"),sQuery(id+"F0.wireOp",EDGE,"E23.0.10"),sQuery(id+"F0.wireOp",EDGE,"E23.0.11"),sQuery(id+"F0.wireOp",EDGE,"E23.0.12"),sQuery(id+"F0.wireOp",EDGE,"E23.0.13"),sQuery(id+"F0.wireOp",EDGE,"E23.0.14"),sQuery(id+"F0.wireOp",EDGE,"E23.0.15"),sQuery(id+"F0.wireOp",EDGE,"E23.0.16"),sQuery(id+"F0.wireOp",EDGE,"E23.0.17"),sQuery(id+"F0.wireOp",EDGE,"E23.0.18"),sQuery(id+"F0.wireOp",EDGE,"E23.0.19"),sQuery(id+"F0.wireOp",EDGE,"E23.0.20"),sQuery(id+"F0.wireOp",EDGE,"E23.0.21"),sQuery(id+"F0.wireOp",EDGE,"E23.0.22"),sQuery(id+"F0.wireOp",EDGE,"E23.0.23"),sQuery(id+"F0.wireOp",EDGE,"E23.0.24"),sQuery(id+"F0.wireOp",EDGE,"E23.0.25"),sQuery(id+"F0.wireOp",EDGE,"E23.0.26"),sQuery(id+"F0.wireOp",EDGE,"E23.0.27"),sQuery(id+"F0.wireOp",EDGE,"E23.0.28"),sQuery(id+"F0.wireOp",EDGE,"E23.0.29"),sQuery(id+"F0.wireOp",EDGE,"E23.0.30"),sQuery(id+"F0.wireOp",EDGE,"E23.0.31"),sQuery(id+"F0.wireOp",EDGE,"E23.0.32"),sQuery(id+"F0.wireOp",EDGE,"E23.0.33"),sQuery(id+"F0.wireOp",EDGE,"E23.0.34"),sQuery(id+"F0.wireOp",EDGE,"E23.0.35"),sQuery(id+"F0.wireOp",EDGE,"E23.0.36"),sQuery(id+"F0.wireOp",EDGE,"E23.0.37"),sQuery(id+"F0.wireOp",EDGE,"E23.0.38"),sQuery(id+"F0.wireOp",EDGE,"E23.0.39"),sQuery(id+"F0.wireOp",EDGE,"E23.0.40"),sQuery(id+"F0.wireOp",EDGE,"E23.0.41"),sQuery(id+"F0.wireOp",EDGE,"E23.0.42"),sQuery(id+"F0.wireOp",EDGE,"E23.0.43"),sQuery(id+"F0.wireOp",EDGE,"E23.0.44"),sQuery(id+"F0.wireOp",EDGE,"E23.0.45"),sQuery(id+"F0.wireOp",EDGE,"E23.0.46"),sQuery(id+"F0.wireOp",EDGE,"E23.0.47"),sQuery(id+"F0.wireOp",EDGE,"E23.0.48"),sQuery(id+"F0.wireOp",EDGE,"E23.0.49"),sQuery(id+"F0.wireOp",EDGE,"E23.0.50"),sQuery(id+"F0.wireOp",EDGE,"E23.0.51"),sQuery(id+"F0.wireOp",EDGE,"E23.0.52"),sQuery(id+"F0.wireOp",EDGE,"E23.0.53"),sQuery(id+"F0.wireOp",EDGE,"E23.0.54"),sQuery(id+"F0.wireOp",EDGE,"E23.0.55"),sQuery(id+"F0.wireOp",EDGE,"E23.0.56"),sQuery(id+"F0.wireOp",EDGE,"E23.0.57"),sQuery(id+"F0.wireOp",EDGE,"E23.0.58"),sQuery(id+"F0.wireOp",EDGE,"E23.0.59"),sQuery(id+"F0.wireOp",EDGE,"E23.0.60"),sQuery(id+"F0.wireOp",EDGE,"E23.0.61"),sQuery(id+"F0.wireOp",EDGE,"E23.0.62"),sQuery(id+"F0.wireOp",EDGE,"E23.0.63"),sQuery(id+"F0.wireOp",EDGE,"E23.0.64"),sQuery(id+"F0.wireOp",EDGE,"E23.0.65"),sQuery(id+"F0.wireOp",EDGE,"E23.0.66"),sQuery(id+"F0.wireOp",EDGE,"E23.0.67"),sQuery(id+"F0.wireOp",EDGE,"E23.0.68"),sQuery(id+"F0.wireOp",EDGE,"E23.0.69"),sQuery(id+"F0.wireOp",EDGE,"E23.0.70"),sQuery(id+"F0.wireOp",EDGE,"E23.0.71"),sQuery(id+"F0.wireOp",EDGE,"E23.0.72"),sQuery(id+"F0.wireOp",EDGE,"E23.0.73"),sQuery(id+"F0.wireOp",EDGE,"E23.0.74"),sQuery(id+"F0.wireOp",EDGE,"E23.0.75"),sQuery(id+"F0.wireOp",EDGE,"E23.0.76"),sQuery(id+"F0.wireOp",EDGE,"E23.0.77"),sQuery(id+"F0.wireOp",EDGE,"E23.0.78"),sQuery(id+"F0.wireOp",EDGE,"E23.0.79"),sQuery(id+"F0.wireOp",EDGE,"E23.0.80"),sQuery(id+"F0.wireOp",EDGE,"E23.0.81"),sQuery(id+"F0.wireOp",EDGE,"E24.0.0"),sQuery(id+"F0.wireOp",EDGE,"E24.0.1"),sQuery(id+"F0.wireOp",EDGE,"E24.0.2"),sQuery(id+"F0.wireOp",EDGE,"E24.0.3"),sQuery(id+"F0.wireOp",EDGE,"E24.0.4"),sQuery(id+"F0.wireOp",EDGE,"E24.0.5"),sQuery(id+"F0.wireOp",EDGE,"E24.0.6"),sQuery(id+"F0.wireOp",EDGE,"E24.0.7"),sQuery(id+"F0.wireOp",EDGE,"E24.0.8"),sQuery(id+"F0.wireOp",EDGE,"E24.0.9"),sQuery(id+"F0.wireOp",EDGE,"E24.0.10"),sQuery(id+"F0.wireOp",EDGE,"E24.0.11"),sQuery(id+"F0.wireOp",EDGE,"E24.0.12"),sQuery(id+"F0.wireOp",EDGE,"E24.0.13"),sQuery(id+"F0.wireOp",EDGE,"E24.0.14"),sQuery(id+"F0.wireOp",EDGE,"E24.0.15"),sQuery(id+"F0.wireOp",EDGE,"E24.0.16"),sQuery(id+"F0.wireOp",EDGE,"E24.0.17"),sQuery(id+"F0.wireOp",EDGE,"E24.0.18"),sQuery(id+"F0.wireOp",EDGE,"E24.0.19"),sQuery(id+"F0.wireOp",EDGE,"E24.0.20"),sQuery(id+"F0.wireOp",EDGE,"E24.0.21"),sQuery(id+"F0.wireOp",EDGE,"E24.0.22"),sQuery(id+"F0.wireOp",EDGE,"E24.0.23"),sQuery(id+"F0.wireOp",EDGE,"E24.0.24"),sQuery(id+"F0.wireOp",EDGE,"E24.0.25"),sQuery(id+"F0.wireOp",EDGE,"E24.0.26"),sQuery(id+"F0.wireOp",EDGE,"E24.0.27"),sQuery(id+"F0.wireOp",EDGE,"E24.0.28"),sQuery(id+"F0.wireOp",EDGE,"E24.0.29"),sQuery(id+"F0.wireOp",EDGE,"E24.0.30"),sQuery(id+"F0.wireOp",EDGE,"E24.0.31"),sQuery(id+"F0.wireOp",EDGE,"E24.0.32"),sQuery(id+"F0.wireOp",EDGE,"E24.0.33"),sQuery(id+"F0.wireOp",EDGE,"E24.0.34"),sQuery(id+"F0.wireOp",EDGE,"E24.0.35"),sQuery(id+"F0.wireOp",EDGE,"E24.0.36"),sQuery(id+"F0.wireOp",EDGE,"E24.0.37"),sQuery(id+"F0.wireOp",EDGE,"E24.0.38"),sQuery(id+"F0.wireOp",EDGE,"E24.0.39"),sQuery(id+"F0.wireOp",EDGE,"E24.0.40"),sQuery(id+"F0.wireOp",EDGE,"E24.0.41"),sQuery(id+"F0.wireOp",EDGE,"E24.0.42"),sQuery(id+"F0.wireOp",EDGE,"E24.0.43"),sQuery(id+"F0.wireOp",EDGE,"E24.0.44"),sQuery(id+"F0.wireOp",EDGE,"E24.0.45"),sQuery(id+"F0.wireOp",EDGE,"E24.0.46"),sQuery(id+"F0.wireOp",EDGE,"E24.0.47"),sQuery(id+"F0.wireOp",EDGE,"E24.0.48"),sQuery(id+"F0.wireOp",EDGE,"E24.0.49"),sQuery(id+"F0.wireOp",EDGE,"E24.0.50"),sQuery(id+"F0.wireOp",EDGE,"E24.0.51"),sQuery(id+"F0.wireOp",EDGE,"E24.0.52"),sQuery(id+"F0.wireOp",EDGE,"E24.0.53"),sQuery(id+"F0.wireOp",EDGE,"E24.0.54"),sQuery(id+"F0.wireOp",EDGE,"E24.0.55"),sQuery(id+"F0.wireOp",EDGE,"E24.0.56"),sQuery(id+"F0.wireOp",EDGE,"E24.0.57"),sQuery(id+"F0.wireOp",EDGE,"E24.0.58"),sQuery(id+"F0.wireOp",EDGE,"E24.0.59"),sQuery(id+"F0.wireOp",EDGE,"E24.0.60"),sQuery(id+"F0.wireOp",EDGE,"E24.0.61"),sQuery(id+"F0.wireOp",EDGE,"E24.0.62"),sQuery(id+"F0.wireOp",EDGE,"E24.0.63"),sQuery(id+"F0.wireOp",EDGE,"E24.0.64"),sQuery(id+"F0.wireOp",EDGE,"E24.0.65"),sQuery(id+"F0.wireOp",EDGE,"E24.0.66"),sQuery(id+"F0.wireOp",EDGE,"E24.0.67"),sQuery(id+"F0.wireOp",EDGE,"E24.0.68"),sQuery(id+"F0.wireOp",EDGE,"E24.0.69"),sQuery(id+"F0.wireOp",EDGE,"E24.0.70"),sQuery(id+"F0.wireOp",EDGE,"E24.0.71"),sQuery(id+"F0.wireOp",EDGE,"E25.0.0"),sQuery(id+"F0.wireOp",EDGE,"E25.0.1"),sQuery(id+"F0.wireOp",EDGE,"E25.0.2"),sQuery(id+"F0.wireOp",EDGE,"E25.0.3"),sQuery(id+"F0.wireOp",EDGE,"E25.0.4"),sQuery(id+"F0.wireOp",EDGE,"E25.0.5"),sQuery(id+"F0.wireOp",EDGE,"E25.0.6"),sQuery(id+"F0.wireOp",EDGE,"E25.0.7"),sQuery(id+"F0.wireOp",EDGE,"E25.0.8"),sQuery(id+"F0.wireOp",EDGE,"E25.0.9"),sQuery(id+"F0.wireOp",EDGE,"E25.0.10"),sQuery(id+"F0.wireOp",EDGE,"E25.0.11"),sQuery(id+"F0.wireOp",EDGE,"E25.0.12"),sQuery(id+"F0.wireOp",EDGE,"E25.0.13"),sQuery(id+"F0.wireOp",EDGE,"E25.0.14"),sQuery(id+"F0.wireOp",EDGE,"E25.0.15"),sQuery(id+"F0.wireOp",EDGE,"E25.0.16"),sQuery(id+"F0.wireOp",EDGE,"E25.0.17"),sQuery(id+"F0.wireOp",EDGE,"E25.0.18"),sQuery(id+"F0.wireOp",EDGE,"E25.0.19"),sQuery(id+"F0.wireOp",EDGE,"E25.0.20"),sQuery(id+"F0.wireOp",EDGE,"E25.0.21"),sQuery(id+"F0.wireOp",EDGE,"E25.0.22"),sQuery(id+"F0.wireOp",EDGE,"E25.0.23"),sQuery(id+"F0.wireOp",EDGE,"E25.0.24"),sQuery(id+"F0.wireOp",EDGE,"E25.0.25"),sQuery(id+"F0.wireOp",EDGE,"E25.0.26"),sQuery(id+"F0.wireOp",EDGE,"E25.0.27"),sQuery(id+"F0.wireOp",EDGE,"E25.0.28"),sQuery(id+"F0.wireOp",EDGE,"E25.0.29"),sQuery(id+"F0.wireOp",EDGE,"E25.0.30"),sQuery(id+"F0.wireOp",EDGE,"E25.0.31"),sQuery(id+"F0.wireOp",EDGE,"E25.0.32"),sQuery(id+"F0.wireOp",EDGE,"E25.0.33"),sQuery(id+"F0.wireOp",EDGE,"E25.0.34"),sQuery(id+"F0.wireOp",EDGE,"E25.0.35"),sQuery(id+"F0.wireOp",EDGE,"E25.0.36"),sQuery(id+"F0.wireOp",EDGE,"E25.0.37"),sQuery(id+"F0.wireOp",EDGE,"E25.0.38"),sQuery(id+"F0.wireOp",EDGE,"E25.0.39"),sQuery(id+"F0.wireOp",EDGE,"E25.0.40"),sQuery(id+"F0.wireOp",EDGE,"E25.0.41"),sQuery(id+"F0.wireOp",EDGE,"E25.0.42"),sQuery(id+"F0.wireOp",EDGE,"E25.0.43"),sQuery(id+"F0.wireOp",EDGE,"E25.0.44"),sQuery(id+"F0.wireOp",EDGE,"E25.0.45"),sQuery(id+"F0.wireOp",EDGE,"E25.0.46"),sQuery(id+"F0.wireOp",EDGE,"E25.0.47"),sQuery(id+"F0.wireOp",EDGE,"E25.0.48"),sQuery(id+"F0.wireOp",EDGE,"E25.0.49"),sQuery(id+"F0.wireOp",EDGE,"E25.0.50"),sQuery(id+"F0.wireOp",EDGE,"E25.0.51"),sQuery(id+"F0.wireOp",EDGE,"E25.0.52"),sQuery(id+"F0.wireOp",EDGE,"E25.0.53"),sQuery(id+"F0.wireOp",EDGE,"E25.0.54"),sQuery(id+"F0.wireOp",EDGE,"E25.0.55"),sQuery(id+"F0.wireOp",EDGE,"E25.0.56"),sQuery(id+"F0.wireOp",EDGE,"E25.0.57"),sQuery(id+"F0.wireOp",EDGE,"E25.0.58"),sQuery(id+"F0.wireOp",EDGE,"E25.0.59"),sQuery(id+"F0.wireOp",EDGE,"E25.0.60"),sQuery(id+"F0.wireOp",EDGE,"E25.0.61"),sQuery(id+"F0.wireOp",EDGE,"E25.0.62"),sQuery(id+"F0.wireOp",EDGE,"E25.0.63"),sQuery(id+"F0.wireOp",EDGE,"E25.0.64"),sQuery(id+"F0.wireOp",EDGE,"E25.0.65"),sQuery(id+"F0.wireOp",EDGE,"E25.0.66"),sQuery(id+"F0.wireOp",EDGE,"E25.0.67"),sQuery(id+"F0.wireOp",EDGE,"E25.0.68"),sQuery(id+"F0.wireOp",EDGE,"E25.0.69"),sQuery(id+"F0.wireOp",EDGE,"E25.0.70"),sQuery(id+"F0.wireOp",EDGE,"E25.0.71"),sQuery(id+"F0.wireOp",EDGE,"E25.0.72"),sQuery(id+"F0.wireOp",EDGE,"E25.0.73"),sQuery(id+"F0.wireOp",EDGE,"E26.0.0"),sQuery(id+"F0.wireOp",EDGE,"E26.0.1"),sQuery(id+"F0.wireOp",EDGE,"E26.0.2"),sQuery(id+"F0.wireOp",EDGE,"E26.0.3"),sQuery(id+"F0.wireOp",EDGE,"E26.0.4"),sQuery(id+"F0.wireOp",EDGE,"E26.0.5"),sQuery(id+"F0.wireOp",EDGE,"E26.0.6"),sQuery(id+"F0.wireOp",EDGE,"E27.0.0"),sQuery(id+"F0.wireOp",EDGE,"E27.0.1"),sQuery(id+"F0.wireOp",EDGE,"E27.0.2"),sQuery(id+"F0.wireOp",EDGE,"E27.0.3"),sQuery(id+"F0.wireOp",EDGE,"E27.0.4"),sQuery(id+"F0.wireOp",EDGE,"E27.0.5"),sQuery(id+"F0.wireOp",EDGE,"E27.0.6"),sQuery(id+"F0.wireOp",EDGE,"E27.0.7"),sQuery(id+"F0.wireOp",EDGE,"E27.0.8"),sQuery(id+"F0.wireOp",EDGE,"E27.0.9"),sQuery(id+"F0.wireOp",EDGE,"E27.0.10"),sQuery(id+"F0.wireOp",EDGE,"E27.0.11"),sQuery(id+"F0.wireOp",EDGE,"E27.0.12"),sQuery(id+"F0.wireOp",EDGE,"E27.0.13"),sQuery(id+"F0.wireOp",EDGE,"E27.0.14"),sQuery(id+"F0.wireOp",EDGE,"E27.0.15"),sQuery(id+"F0.wireOp",EDGE,"E27.0.16"),sQuery(id+"F0.wireOp",EDGE,"E27.0.17"),sQuery(id+"F0.wireOp",EDGE,"E27.0.18"),sQuery(id+"F0.wireOp",EDGE,"E27.0.19"),sQuery(id+"F0.wireOp",EDGE,"E27.0.20"),sQuery(id+"F0.wireOp",EDGE,"E27.0.21"),sQuery(id+"F0.wireOp",EDGE,"E27.0.22"),sQuery(id+"F0.wireOp",EDGE,"E27.0.23"),sQuery(id+"F0.wireOp",EDGE,"E27.0.24"),sQuery(id+"F0.wireOp",EDGE,"E27.0.25"),sQuery(id+"F0.wireOp",EDGE,"E27.0.26"),sQuery(id+"F0.wireOp",EDGE,"E27.0.27"),sQuery(id+"F0.wireOp",EDGE,"E27.0.28"),sQuery(id+"F0.wireOp",EDGE,"E27.0.29"),sQuery(id+"F0.wireOp",EDGE,"E27.0.30"),sQuery(id+"F0.wireOp",EDGE,"E27.0.31"),sQuery(id+"F0.wireOp",EDGE,"E27.0.32"),sQuery(id+"F0.wireOp",EDGE,"E27.0.33"),sQuery(id+"F0.wireOp",EDGE,"E27.0.34"),sQuery(id+"F0.wireOp",EDGE,"E27.0.35"),sQuery(id+"F0.wireOp",EDGE,"E27.0.36"),sQuery(id+"F0.wireOp",EDGE,"E27.0.37"),sQuery(id+"F0.wireOp",EDGE,"E27.0.38"),sQuery(id+"F0.wireOp",EDGE,"E27.0.39"),sQuery(id+"F0.wireOp",EDGE,"E27.0.40"),sQuery(id+"F0.wireOp",EDGE,"E27.0.41"),sQuery(id+"F0.wireOp",EDGE,"E27.0.42"),sQuery(id+"F0.wireOp",EDGE,"E27.0.43"),sQuery(id+"F0.wireOp",EDGE,"E27.0.44"),sQuery(id+"F0.wireOp",EDGE,"E27.0.45"),sQuery(id+"F0.wireOp",EDGE,"E27.0.46"),sQuery(id+"F0.wireOp",EDGE,"E27.0.47"),sQuery(id+"F0.wireOp",EDGE,"E27.0.48"),sQuery(id+"F0.wireOp",EDGE,"E27.0.49"),sQuery(id+"F0.wireOp",EDGE,"E27.0.50"),sQuery(id+"F0.wireOp",EDGE,"E27.0.51"),sQuery(id+"F0.wireOp",EDGE,"E27.0.52"),sQuery(id+"F0.wireOp",EDGE,"E27.0.53"),sQuery(id+"F0.wireOp",EDGE,"E27.0.54"),sQuery(id+"F0.wireOp",EDGE,"E27.0.55"),sQuery(id+"F0.wireOp",EDGE,"E27.0.56"),sQuery(id+"F0.wireOp",EDGE,"E27.0.57"),sQuery(id+"F0.wireOp",EDGE,"E27.0.58"),sQuery(id+"F0.wireOp",EDGE,"E27.0.59"),sQuery(id+"F0.wireOp",EDGE,"E27.0.60"),sQuery(id+"F0.wireOp",EDGE,"E27.0.61"),sQuery(id+"F0.wireOp",EDGE,"E27.0.62"),sQuery(id+"F0.wireOp",EDGE,"E27.0.63"),sQuery(id+"F0.wireOp",EDGE,"E27.0.64"),sQuery(id+"F0.wireOp",EDGE,"E27.0.65"),sQuery(id+"F0.wireOp",EDGE,"E27.0.66"),sQuery(id+"F0.wireOp",EDGE,"E27.0.67"),sQuery(id+"F0.wireOp",EDGE,"E27.0.68"),sQuery(id+"F0.wireOp",EDGE,"E27.0.69"),sQuery(id+"F0.wireOp",EDGE,"E27.0.70"),sQuery(id+"F0.wireOp",EDGE,"E27.0.71"),sQuery(id+"F0.wireOp",EDGE,"E27.0.72"),sQuery(id+"F0.wireOp",EDGE,"E27.0.73"),sQuery(id+"F0.wireOp",EDGE,"E28"),sQuery(id+"F0.wireOp",EDGE,"E29"),sQuery(id+"F0.wireOp",EDGE,"05731d6a-1b1d-4da3-b72a-bea029b93d1c.sketch_text.stroke-0"),sQuery(id+"F0.wireOp",EDGE,"05731d6a-1b1d-4da3-b72a-bea029b93d1c.sketch_text.stroke-1"),sQuery(id+"F0.wireOp",EDGE,"05731d6a-1b1d-4da3-b72a-bea029b93d1c.sketch_text.stroke-2"),sQuery(id+"F0.wireOp",EDGE,"05731d6a-1b1d-4da3-b72a-bea029b93d1c.sketch_text.stroke-3"),sQuery(id+"F0.wireOp",EDGE,"05731d6a-1b1d-4da3-b72a-bea029b93d1c.sketch_text.stroke-4"),sQuery(id+"F0.wireOp",EDGE,"05731d6a-1b1d-4da3-b72a-bea029b93d1c.sketch_text.stroke-5"),sQuery(id+"F0.wireOp",EDGE,"05731d6a-1b1d-4da3-b72a-bea029b93d1c.sketch_text.stroke-6"),sQuery(id+"F0.wireOp",EDGE,"05731d6a-1b1d-4da3-b72a-bea029b93d1c.sketch_text.stroke-14"),sQuery(id+"F0.wireOp",EDGE,"05731d6a-1b1d-4da3-b72a-bea029b93d1c.sketch_text.stroke-15"),sQuery(id+"F0.wireOp",EDGE,"05731d6a-1b1d-4da3-b72a-bea029b93d1c.sketch_text.stroke-16"),sQuery(id+"F0.wireOp",EDGE,"05731d6a-1b1d-4da3-b72a-bea029b93d1c.sketch_text.stroke-17"),sQuery(id+"F0.wireOp",EDGE,"05731d6a-1b1d-4da3-b72a-bea029b93d1c.sketch_text.stroke-18"),sQuery(id+"F0.wireOp",EDGE,"05731d6a-1b1d-4da3-b72a-bea029b93d1c.sketch_text.stroke-19"),sQuery(id+"F0.wireOp",EDGE,"05731d6a-1b1d-4da3-b72a-bea029b93d1c.sketch_text.stroke-20"),sQuery(id+"F0.wireOp",EDGE,"05731d6a-1b1d-4da3-b72a-bea029b93d1c.sketch_text.stroke-21"),sQuery(id+"F0.wireOp",EDGE,"05731d6a-1b1d-4da3-b72a-bea029b93d1c.sketch_text.stroke-22"),sQuery(id+"F0.wireOp",EDGE,"05731d6a-1b1d-4da3-b72a-bea029b93d1c.sketch_text.stroke-23"),sQuery(id+"F0.wireOp",EDGE,"05731d6a-1b1d-4da3-b72a-bea029b93d1c.sketch_text.stroke-24"),sQuery(id+"F0.wireOp",EDGE,"05731d6a-1b1d-4da3-b72a-bea029b93d1c.sketch_text.stroke-25"),sQuery(id+"F0.wireOp",EDGE,"05731d6a-1b1d-4da3-b72a-bea029b93d1c.sketch_text.stroke-26"),sQuery(id+"F0.wireOp",EDGE,"05731d6a-1b1d-4da3-b72a-bea029b93d1c.sketch_text.stroke-27"),sQuery(id+"F0.wireOp",EDGE,"05731d6a-1b1d-4da3-b72a-bea029b93d1c.sketch_text.stroke-33"),sQuery(id+"F0.wireOp",EDGE,"05731d6a-1b1d-4da3-b72a-bea029b93d1c.sketch_text.stroke-34"),sQuery(id+"F0.wireOp",EDGE,"05731d6a-1b1d-4da3-b72a-bea029b93d1c.sketch_text.stroke-35"),sQuery(id+"F0.wireOp",EDGE,"05731d6a-1b1d-4da3-b72a-bea029b93d1c.sketch_text.stroke-36"),sQuery(id+"F0.wireOp",EDGE,"05731d6a-1b1d-4da3-b72a-bea029b93d1c.sketch_text.stroke-37"),sQuery(id+"F0.wireOp",EDGE,"05731d6a-1b1d-4da3-b72a-bea029b93d1c.sketch_text.stroke-38"),sQuery(id+"F0.wireOp",EDGE,"05731d6a-1b1d-4da3-b72a-bea029b93d1c.sketch_text.stroke-39"),sQuery(id+"F0.wireOp",EDGE,"05731d6a-1b1d-4da3-b72a-bea029b93d1c.sketch_text.stroke-40"),sQuery(id+"F0.wireOp",EDGE,"05731d6a-1b1d-4da3-b72a-bea029b93d1c.sketch_text.stroke-41"),sQuery(id+"F0.wireOp",EDGE,"05731d6a-1b1d-4da3-b72a-bea029b93d1c.sketch_text.stroke-42"),sQuery(id+"F0.wireOp",EDGE,"05731d6a-1b1d-4da3-b72a-bea029b93d1c.sketch_text.stroke-43"),sQuery(id+"F0.wireOp",EDGE,"05731d6a-1b1d-4da3-b72a-bea029b93d1c.sketch_text.stroke-44"),sQuery(id+"F0.wireOp",EDGE,"05731d6a-1b1d-4da3-b72a-bea029b93d1c.sketch_text.stroke-45"),sQuery(id+"F0.wireOp",EDGE,"05731d6a-1b1d-4da3-b72a-bea029b93d1c.sketch_text.stroke-46"),sQuery(id+"F0.wireOp",EDGE,"05731d6a-1b1d-4da3-b72a-bea029b93d1c.sketch_text.stroke-47"),sQuery(id+"F0.wireOp",EDGE,"05731d6a-1b1d-4da3-b72a-bea029b93d1c.sketch_text.stroke-48"),sQuery(id+"F0.wireOp",EDGE,"05731d6a-1b1d-4da3-b72a-bea029b93d1c.sketch_text.stroke-49"),sQuery(id+"F0.wireOp",EDGE,"05731d6a-1b1d-4da3-b72a-bea029b93d1c.sketch_text.stroke-50"),sQuery(id+"F0.wireOp",EDGE,"05731d6a-1b1d-4da3-b72a-bea029b93d1c.sketch_text.stroke-51"),sQuery(id+"F0.wireOp",EDGE,"05731d6a-1b1d-4da3-b72a-bea029b93d1c.sketch_text.stroke-52"),sQuery(id+"F0.wireOp",EDGE,"05731d6a-1b1d-4da3-b72a-bea029b93d1c.sketch_text.stroke-53"),sQuery(id+"F0.wireOp",EDGE,"05731d6a-1b1d-4da3-b72a-bea029b93d1c.sketch_text.stroke-54"),sQuery(id+"F0.wireOp",EDGE,"05731d6a-1b1d-4da3-b72a-bea029b93d1c.sketch_text.stroke-55"),sQuery(id+"F0.wireOp",EDGE,"05731d6a-1b1d-4da3-b72a-bea029b93d1c.sketch_text.stroke-56"),sQuery(id+"F0.wireOp",EDGE,"05731d6a-1b1d-4da3-b72a-bea029b93d1c.sketch_text.stroke-57"),sQuery(id+"F0.wireOp",EDGE,"05731d6a-1b1d-4da3-b72a-bea029b93d1c.sketch_text.stroke-58"),sQuery(id+"F0.wireOp",EDGE,"05731d6a-1b1d-4da3-b72a-bea029b93d1c.sketch_text.stroke-59"),sQuery(id+"F0.wireOp",EDGE,"05731d6a-1b1d-4da3-b72a-bea029b93d1c.sketch_text.stroke-60"),sQuery(id+"F0.wireOp",EDGE,"05731d6a-1b1d-4da3-b72a-bea029b93d1c.sketch_text.stroke-61"),sQuery(id+"F0.wireOp",EDGE,"05731d6a-1b1d-4da3-b72a-bea029b93d1c.sketch_text.stroke-62"),sQuery(id+"F0.wireOp",EDGE,"05731d6a-1b1d-4da3-b72a-bea029b93d1c.sketch_text.stroke-63"),sQuery(id+"F0.wireOp",EDGE,"05731d6a-1b1d-4da3-b72a-bea029b93d1c.sketch_text.stroke-64"),sQuery(id+"F0.wireOp",EDGE,"05731d6a-1b1d-4da3-b72a-bea029b93d1c.sketch_text.stroke-65"),sQuery(id+"F0.wireOp",EDGE,"05731d6a-1b1d-4da3-b72a-bea029b93d1c.sketch_text.stroke-66"),sQuery(id+"F0.wireOp",EDGE,"05731d6a-1b1d-4da3-b72a-bea029b93d1c.sketch_text.stroke-67"),sQuery(id+"F0.wireOp",EDGE,"05731d6a-1b1d-4da3-b72a-bea029b93d1c.sketch_text.stroke-68"),sQuery(id+"F0.wireOp",EDGE,"05731d6a-1b1d-4da3-b72a-bea029b93d1c.sketch_text.stroke-69"),sQuery(id+"F0.wireOp",EDGE,"05731d6a-1b1d-4da3-b72a-bea029b93d1c.sketch_text.stroke-70"),sQuery(id+"F0.wireOp",EDGE,"05731d6a-1b1d-4da3-b72a-bea029b93d1c.sketch_text.stroke-71"),sQuery(id+"F0.wireOp",EDGE,"05731d6a-1b1d-4da3-b72a-bea029b93d1c.sketch_text.stroke-72"),sQuery(id+"F0.wireOp",EDGE,"05731d6a-1b1d-4da3-b72a-bea029b93d1c.sketch_text.stroke-73"),sQuery(id+"F0.wireOp",EDGE,"05731d6a-1b1d-4da3-b72a-bea029b93d1c.sketch_text.stroke-74"),sQuery(id+"F0.wireOp",EDGE,"05731d6a-1b1d-4da3-b72a-bea029b93d1c.sketch_text.stroke-75"),sQuery(id+"F0.wireOp",EDGE,"05731d6a-1b1d-4da3-b72a-bea029b93d1c.sketch_text.stroke-76"),sQuery(id+"F0.wireOp",EDGE,"05731d6a-1b1d-4da3-b72a-bea029b93d1c.sketch_text.stroke-77"),sQuery(id+"F0.wireOp",EDGE,"05731d6a-1b1d-4da3-b72a-bea029b93d1c.sketch_text.stroke-78"),sQuery(id+"F0.wireOp",EDGE,"05731d6a-1b1d-4da3-b72a-bea029b93d1c.sketch_text.stroke-79"),sQuery(id+"F0.wireOp",EDGE,"05731d6a-1b1d-4da3-b72a-bea029b93d1c.sketch_text.stroke-80"),sQuery(id+"F0.wireOp",EDGE,"05731d6a-1b1d-4da3-b72a-bea029b93d1c.sketch_text.stroke-81"),sQuery(id+"F0.wireOp",EDGE,"05731d6a-1b1d-4da3-b72a-bea029b93d1c.sketch_text.stroke-82"),sQuery(id+"F0.wireOp",EDGE,"05731d6a-1b1d-4da3-b72a-bea029b93d1c.sketch_text.stroke-83"),sQuery(id+"F0.wireOp",EDGE,"05731d6a-1b1d-4da3-b72a-bea029b93d1c.sketch_text.stroke-84"),sQuery(id+"F0.wireOp",EDGE,"05731d6a-1b1d-4da3-b72a-bea029b93d1c.sketch_text.stroke-85"),sQuery(id+"F0.wireOp",EDGE,"05731d6a-1b1d-4da3-b72a-bea029b93d1c.sketch_text.stroke-86"),sQuery(id+"F0.wireOp",EDGE,"05731d6a-1b1d-4da3-b72a-bea029b93d1c.sketch_text.stroke-87"),sQuery(id+"F0.wireOp",EDGE,"05731d6a-1b1d-4da3-b72a-bea029b93d1c.sketch_text.stroke-88"),sQuery(id+"F0.wireOp",EDGE,"05731d6a-1b1d-4da3-b72a-bea029b93d1c.sketch_text.stroke-89"),sQuery(id+"F0.wireOp",EDGE,"05731d6a-1b1d-4da3-b72a-bea029b93d1c.sketch_text.stroke-90"),sQuery(id+"F0.wireOp",EDGE,"05731d6a-1b1d-4da3-b72a-bea029b93d1c.sketch_text.stroke-91"),sQuery(id+"F0.wireOp",EDGE,"05731d6a-1b1d-4da3-b72a-bea029b93d1c.sketch_text.stroke-92"),sQuery(id+"F0.wireOp",EDGE,"05731d6a-1b1d-4da3-b72a-bea029b93d1c.sketch_text.stroke-93"),sQuery(id+"F0.wireOp",EDGE,"05731d6a-1b1d-4da3-b72a-bea029b93d1c.sketch_text.stroke-94"),sQuery(id+"F0.wireOp",EDGE,"05731d6a-1b1d-4da3-b72a-bea029b93d1c.sketch_text.stroke-95"),sQuery(id+"F0.wireOp",EDGE,"05731d6a-1b1d-4da3-b72a-bea029b93d1c.sketch_text.stroke-96"),sQuery(id+"F0.wireOp",EDGE,"05731d6a-1b1d-4da3-b72a-bea029b93d1c.sketch_text.stroke-97"),sQuery(id+"F0.wireOp",EDGE,"05731d6a-1b1d-4da3-b72a-bea029b93d1c.sketch_text.stroke-98"),sQuery(id+"F0.wireOp",EDGE,"05731d6a-1b1d-4da3-b72a-bea029b93d1c.sketch_text.stroke-99"),sQuery(id+"F0.wireOp",EDGE,"05731d6a-1b1d-4da3-b72a-bea029b93d1c.sketch_text.stroke-100"),sQuery(id+"F0.wireOp",EDGE,"05731d6a-1b1d-4da3-b72a-bea029b93d1c.sketch_text.stroke-101"),sQuery(id+"F0.wireOp",EDGE,"05731d6a-1b1d-4da3-b72a-bea029b93d1c.sketch_text.stroke-102"),sQuery(id+"F0.wireOp",EDGE,"05731d6a-1b1d-4da3-b72a-bea029b93d1c.sketch_text.stroke-103"),sQuery(id+"F0.wireOp",EDGE,"05731d6a-1b1d-4da3-b72a-bea029b93d1c.sketch_text.stroke-104"),sQuery(id+"F0.wireOp",EDGE,"05731d6a-1b1d-4da3-b72a-bea029b93d1c.sketch_text.stroke-105"),sQuery(id+"F0.wireOp",EDGE,"05731d6a-1b1d-4da3-b72a-bea029b93d1c.sketch_text.stroke-106"),sQuery(id+"F0.wireOp",EDGE,"05731d6a-1b1d-4da3-b72a-bea029b93d1c.sketch_text.stroke-107"),sQuery(id+"F0.wireOp",EDGE,"05731d6a-1b1d-4da3-b72a-bea029b93d1c.sketch_text.stroke-108"),sQuery(id+"F0.wireOp",EDGE,"05731d6a-1b1d-4da3-b72a-bea029b93d1c.sketch_text.stroke-109"),sQuery(id+"F0.wireOp",EDGE,"05731d6a-1b1d-4da3-b72a-bea029b93d1c.sketch_text.stroke-110"),sQuery(id+"F0.wireOp",EDGE,"05731d6a-1b1d-4da3-b72a-bea029b93d1c.sketch_text.stroke-111"),sQuery(id+"F0.wireOp",EDGE,"05731d6a-1b1d-4da3-b72a-bea029b93d1c.sketch_text.stroke-112"),sQuery(id+"F0.wireOp",EDGE,"05731d6a-1b1d-4da3-b72a-bea029b93d1c.sketch_text.stroke-113"),sQuery(id+"F0.wireOp",EDGE,"05731d6a-1b1d-4da3-b72a-bea029b93d1c.sketch_text.stroke-114"),sQuery(id+"F0.wireOp",EDGE,"05731d6a-1b1d-4da3-b72a-bea029b93d1c.sketch_text.stroke-115"),sQuery(id+"F0.wireOp",EDGE,"05731d6a-1b1d-4da3-b72a-bea029b93d1c.sketch_text.stroke-116"),sQuery(id+"F0.wireOp",EDGE,"05731d6a-1b1d-4da3-b72a-bea029b93d1c.sketch_text.stroke-117"),sQuery(id+"F0.wireOp",EDGE,"05731d6a-1b1d-4da3-b72a-bea029b93d1c.sketch_text.stroke-118"),sQuery(id+"F0.wireOp",EDGE,"05731d6a-1b1d-4da3-b72a-bea029b93d1c.sketch_text.stroke-119"),sQuery(id+"F0.wireOp",EDGE,"05731d6a-1b1d-4da3-b72a-bea029b93d1c.sketch_text.stroke-120"),sQuery(id+"F0.wireOp",EDGE,"05731d6a-1b1d-4da3-b72a-bea029b93d1c.sketch_text.stroke-121"),sQuery(id+"F0.wireOp",EDGE,"05731d6a-1b1d-4da3-b72a-bea029b93d1c.sketch_text.stroke-122"),sQuery(id+"F0.wireOp",EDGE,"05731d6a-1b1d-4da3-b72a-bea029b93d1c.sketch_text.stroke-123"),sQuery(id+"F0.wireOp",EDGE,"05731d6a-1b1d-4da3-b72a-bea029b93d1c.sketch_text.stroke-124"),sQuery(id+"F0.wireOp",EDGE,"05731d6a-1b1d-4da3-b72a-bea029b93d1c.sketch_text.stroke-125"),sQuery(id+"F0.wireOp",EDGE,"05731d6a-1b1d-4da3-b72a-bea029b93d1c.sketch_text.stroke-126"),sQuery(id+"F0.wireOp",EDGE,"05731d6a-1b1d-4da3-b72a-bea029b93d1c.sketch_text.stroke-127"),sQuery(id+"F0.wireOp",EDGE,"05731d6a-1b1d-4da3-b72a-bea029b93d1c.sketch_text.stroke-128"),sQuery(id+"F0.wireOp",EDGE,"05731d6a-1b1d-4da3-b72a-bea029b93d1c.sketch_text.stroke-129"),sQuery(id+"F0.wireOp",EDGE,"05731d6a-1b1d-4da3-b72a-bea029b93d1c.sketch_text.stroke-137"),sQuery(id+"F0.wireOp",EDGE,"05731d6a-1b1d-4da3-b72a-bea029b93d1c.sketch_text.stroke-138"),sQuery(id+"F0.wireOp",EDGE,"05731d6a-1b1d-4da3-b72a-bea029b93d1c.sketch_text.stroke-139"),sQuery(id+"F0.wireOp",EDGE,"05731d6a-1b1d-4da3-b72a-bea029b93d1c.sketch_text.stroke-140"),sQuery(id+"F0.wireOp",EDGE,"05731d6a-1b1d-4da3-b72a-bea029b93d1c.sketch_text.stroke-141"),sQuery(id+"F0.wireOp",EDGE,"05731d6a-1b1d-4da3-b72a-bea029b93d1c.sketch_text.stroke-142"),sQuery(id+"F0.wireOp",EDGE,"05731d6a-1b1d-4da3-b72a-bea029b93d1c.sketch_text.stroke-143"),sQuery(id+"F0.wireOp",EDGE,"05731d6a-1b1d-4da3-b72a-bea029b93d1c.sketch_text.stroke-144"),sQuery(id+"F0.wireOp",EDGE,"05731d6a-1b1d-4da3-b72a-bea029b93d1c.sketch_text.stroke-150"),sQuery(id+"F0.wireOp",EDGE,"05731d6a-1b1d-4da3-b72a-bea029b93d1c.sketch_text.stroke-151"),sQuery(id+"F0.wireOp",EDGE,"05731d6a-1b1d-4da3-b72a-bea029b93d1c.sketch_text.stroke-152"),sQuery(id+"F0.wireOp",EDGE,"05731d6a-1b1d-4da3-b72a-bea029b93d1c.sketch_text.stroke-153"),sQuery(id+"F0.wireOp",EDGE,"05731d6a-1b1d-4da3-b72a-bea029b93d1c.sketch_text.stroke-154"),sQuery(id+"F0.wireOp",EDGE,"05731d6a-1b1d-4da3-b72a-bea029b93d1c.sketch_text.stroke-155"),sQuery(id+"F0.wireOp",EDGE,"E30.filletArc"),sQuery(id+"F0.wireOp",EDGE,"E31.filletArc")])],"isStart":false});
            var sketch = newSketch(context, id + "F2", { "sketchPlane" : qUnion([Q0])});
            skText(sketch, "E32", { "text": "Denis GERAL", "fontName": "OpenSans-Regular.ttf"});
            const initialGuessF2  = {"E32": [-0.23018, -0.05397, 1, 0, 0.006]};
            skSetInitialGuess(sketch, initialGuessF2);
            skSolve(sketch);
        }
        {
            var Q0;
            Q0 = qSketchRegion(id + "F2", true);
            extrude(context, id + "F3", {"entities" : qUnion([Q0]), "operationType" : NewBodyOperationType.REMOVE, "oppositeDirection" : true, "depth" : 1 * mm});
        }
    });
